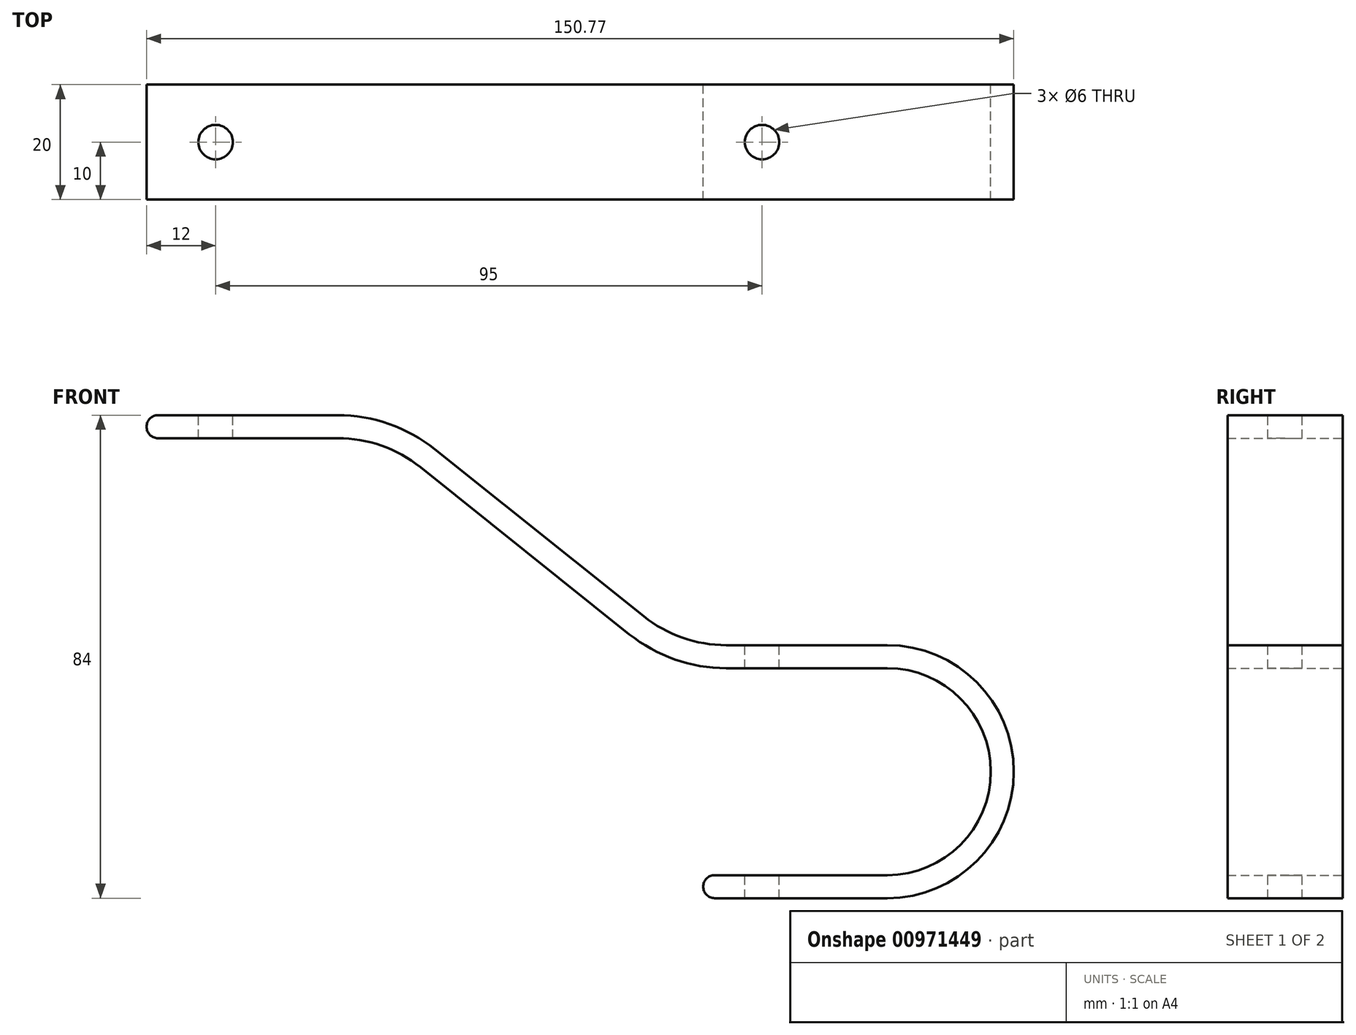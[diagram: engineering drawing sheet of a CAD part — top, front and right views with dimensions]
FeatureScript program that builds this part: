
annotation { "Feature Type Name" : "Feature", "Feature Type Description" : "" }
export const myFeature = defineFeature(function(context is Context, id is Id, definition is map)
    precondition{}
    {
        {
            var Q0;
            Q0=qCreatedBy(makeId("Front.planeOp"),FACE);
            var sketch = newSketch(context, id + "F0", { "sketchPlane" : qUnion([Q0])});
            skLineSegment(sketch, "E0", {"start": v(-15, 40) * mm, "end": v(-65, 40) * mm, "construction": true});
            skLineSegment(sketch, "E1", {"start": v(-65, 40) * mm, "end": v(-65, 80) * mm, "construction": true});
            skLineSegment(sketch, "E2", {"start": v(-21.85, 45.48) * mm, "end": v(-58.15, 74.52) * mm});
            skPoint(sketch, "E3.visualSharp", {"position": v(-15, 40) * mm});
            skArc(sketch, "E3.filletArc", {"start": v(-21.85, 45.48) * mm, "mid": v(-14.5, 41.4) * mm, "end": v(-6.23, 40) * mm});
            skPoint(sketch, "E4.visualSharp", {"position": v(-65, 80) * mm});
            skArc(sketch, "E4.filletArc", {"start": v(-58.15, 74.52) * mm, "mid": v(-65.5, 78.6) * mm, "end": v(-73.77, 80) * mm});
            skLineSegment(sketch, "E5.0", {"start": v(-73.77, 82) * mm, "end": v(-105, 82) * mm});
            skArc(sketch, "E5.1", {"start": v(-56.9, 76.08) * mm, "mid": v(-64.83, 80.48) * mm, "end": v(-73.77, 82) * mm});
            skLineSegment(sketch, "E5.2", {"start": v(-20.6, 47.04) * mm, "end": v(-56.9, 76.08) * mm});
            skArc(sketch, "E5.3", {"start": v(-20.6, 47.04) * mm, "mid": v(-13.84, 43.3) * mm, "end": v(-6.23, 42) * mm});
            skLineSegment(sketch, "E6.0", {"start": v(-73.77, 78) * mm, "end": v(-105, 78) * mm});
            skArc(sketch, "E6.1", {"start": v(-59.4, 72.96) * mm, "mid": v(-66.16, 76.7) * mm, "end": v(-73.77, 78) * mm});
            skLineSegment(sketch, "E6.2", {"start": v(-23.1, 43.92) * mm, "end": v(-59.4, 72.96) * mm});
            skArc(sketch, "E6.3", {"start": v(-23.1, 43.92) * mm, "mid": v(-15.17, 39.52) * mm, "end": v(-6.23, 38) * mm});
            skLineSegment(sketch, "E7", {"start": v(-73.77, 80) * mm, "end": v(-105, 80) * mm});
            skArc(sketch, "E8", {"start": v(-105, 78) * mm, "mid": v(-107, 80) * mm, "end": v(-105, 82) * mm});
            skLineSegment(sketch, "E9", {"start": v(-6.23, 40) * mm, "end": v(1.77, 40) * mm});
            skLineSegment(sketch, "E10", {"start": v(1.77, 40) * mm, "end": v(1.77, 0) * mm, "construction": true});
            skLineSegment(sketch, "E11", {"start": v(1.77, 20) * mm, "end": v(38.92, 20) * mm, "construction": true});
            skLineSegment(sketch, "E12", {"start": v(1.77, 40) * mm, "end": v(21.77, 40) * mm});
            skLineSegment(sketch, "E13", {"start": v(1.77, 0) * mm, "end": v(21.77, 0) * mm});
            skArc(sketch, "E14", {"start": v(21.77, 40) * mm, "mid": v(41.77, 20) * mm, "end": v(21.77, 0) * mm});
            skLineSegment(sketch, "E15", {"start": v(1.77, 0) * mm, "end": v(-8.23, 0) * mm});
            skLineSegment(sketch, "E16.0", {"start": v(1.77, 38) * mm, "end": v(21.77, 38) * mm});
            skLineSegment(sketch, "E16.1", {"start": v(-6.23, 38) * mm, "end": v(1.77, 38) * mm});
            skLineSegment(sketch, "E17.0", {"start": v(1.77, 2) * mm, "end": v(-8.23, 2) * mm});
            skLineSegment(sketch, "E17.1", {"start": v(1.77, 2) * mm, "end": v(21.77, 2) * mm});
            skArc(sketch, "E17.2", {"start": v(21.77, 38) * mm, "mid": v(39.77, 20) * mm, "end": v(21.77, 2) * mm});
            skLineSegment(sketch, "E18.0", {"start": v(1.77, -2) * mm, "end": v(-8.23, -2) * mm});
            skLineSegment(sketch, "E18.1", {"start": v(-6.23, 42) * mm, "end": v(1.77, 42) * mm});
            skLineSegment(sketch, "E18.2", {"start": v(1.77, 42) * mm, "end": v(21.77, 42) * mm});
            skArc(sketch, "E18.3", {"start": v(21.77, 42) * mm, "mid": v(43.77, 20) * mm, "end": v(21.77, -2) * mm});
            skLineSegment(sketch, "E18.4", {"start": v(1.77, -2) * mm, "end": v(21.77, -2) * mm});
            skArc(sketch, "E19", {"start": v(-8.23, -2) * mm, "mid": v(-10.23, 0) * mm, "end": v(-8.23, 2) * mm});
            skSolve(sketch);
        }
        {
            var Q0;
            Q0=makeQuery(id+"F0.imprint","IMPRINT",FACE,{"disambiguationData":[TD([[makeQuery(id+"F0.imprint","IMPRINT",EDGE,{"derivedFrom":sQuery(id+"F0.wireOp",EDGE,"E5.0")}),1.0]])]});
            extrude(context, id + "F1", {"entities" : qUnion([Q0]), "endBound" : BoundingType.SYMMETRIC, "depth" : 20 * mm, "offsetDistance" : 25 * mm});
        }
        {
            var Q0;
            Q0=qCreatedBy(makeId("Top.planeOp"),FACE);
            var sketch = newSketch(context, id + "F2", { "sketchPlane" : qUnion([Q0])});
            skCircle(sketch, "E20", {"center": v(0, 0) * mm, "radius": 3 * mm});
            skLineSegment(sketch, "E21", {"start": v(0, 0) * mm, "end": v(0, 0) * mm});
            skSolve(sketch);
        }
        {
            var Q0;
            Q0 = qSketchRegion(id + "F2", true);
            extrude(context, id + "F3", {"entities" : qUnion([Q0]), "operationType" : NewBodyOperationType.REMOVE, "endBound" : BoundingType.SYMMETRIC, "oppositeDirection" : true, "depth" : 100 * mm, "offsetDistance" : 25 * mm});
        }
        {
            var Q0;
            Q0=makeQuery(id+"F1.opExtrude","SWEPT_FACE",FACE,{"disambiguationData":[OSD([sQuery(id+"F0.wireOp",EDGE,"E5.0")])]});
            var sketch = newSketch(context, id + "F4", { "sketchPlane" : qUnion([Q0])});
            skLineSegment(sketch, "E22.0", {"start": v(-105, -10) * mm, "end": v(-105, 10) * mm, "construction": true});
            skLineSegment(sketch, "E23", {"start": v(-105, 0) * mm, "end": v(-95, 0) * mm, "construction": true});
            skCircle(sketch, "E24", {"center": v(-95, 0) * mm, "radius": 3 * mm});
            skSolve(sketch);
        }
        {
            var Q0;
            Q0 = qSketchRegion(id + "F4", true);
            extrude(context, id + "F5", {"entities" : qUnion([Q0]), "operationType" : NewBodyOperationType.REMOVE, "oppositeDirection" : true, "depth" : 25 * mm, "offsetDistance" : 25 * mm});
        }
    });
